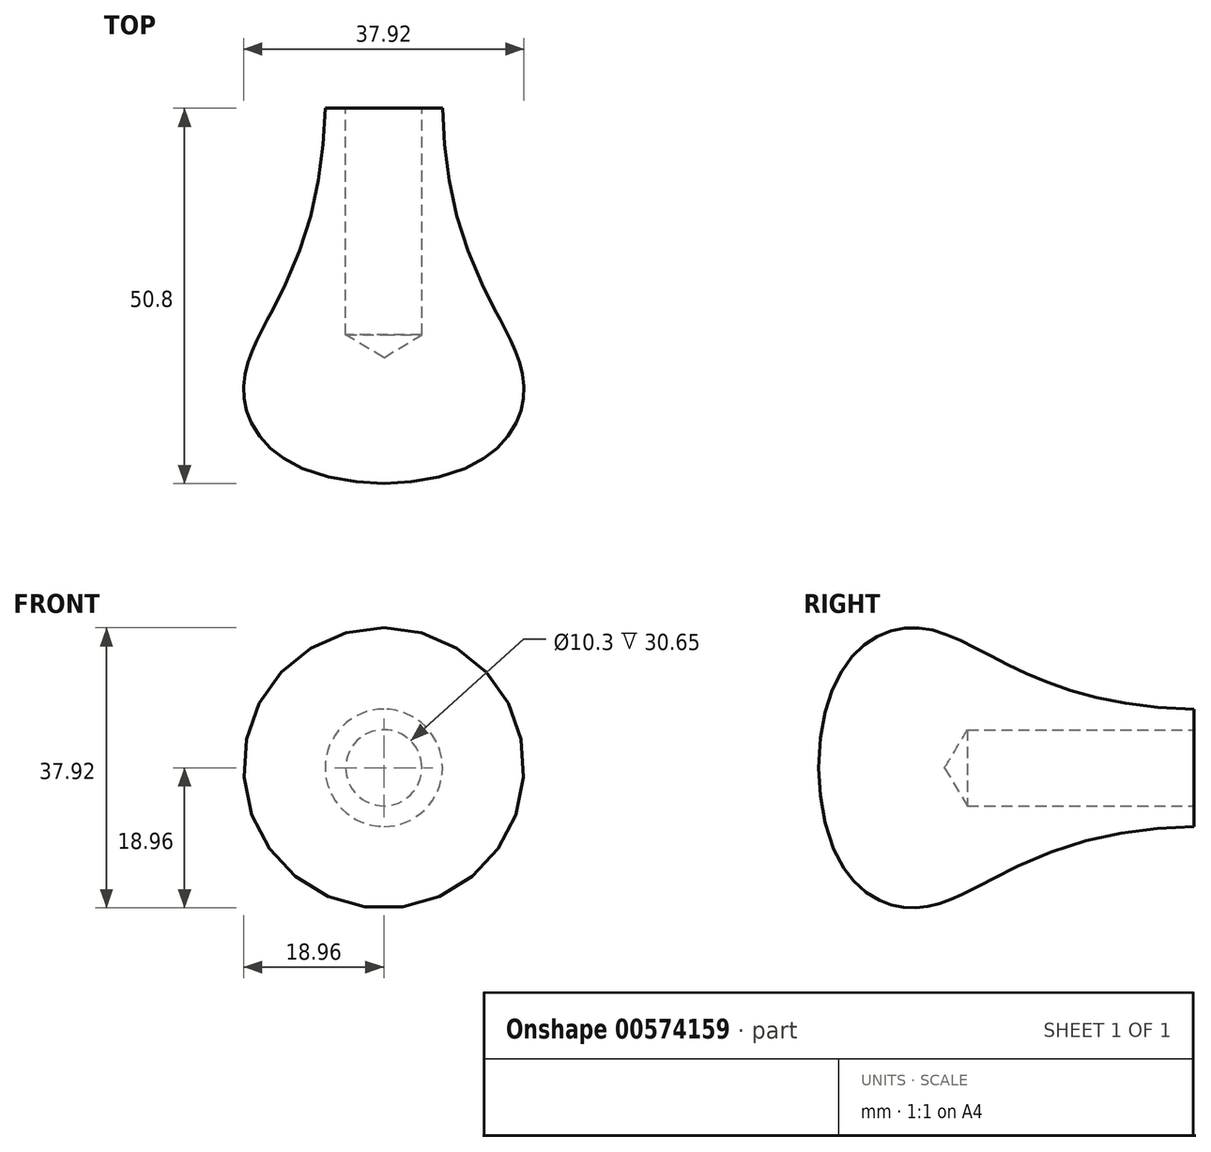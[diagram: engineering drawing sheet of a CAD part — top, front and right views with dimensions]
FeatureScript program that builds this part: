
annotation { "Feature Type Name" : "Feature", "Feature Type Description" : "" }
export const myFeature = defineFeature(function(context is Context, id is Id, definition is map)
    precondition{}
    {
        {
            var Q0;
            Q0=qCreatedBy(makeId("Right.planeOp"),FACE);
            var sketch = newSketch(context, id + "F0", { "sketchPlane" : qUnion([Q0])});
            skLineSegment(sketch, "E0", {"start": v(-50.8, 0) * mm, "end": v(0, 0) * mm});
            skLineSegment(sketch, "E1", {"start": v(0, 0) * mm, "end": v(0, 7.94) * mm});
            skFitSpline(sketch, "E2", {"points": [v(-50.8, 0) * mm, v(-37.12, 18.92) * mm, v(0, 7.94) * mm], "startDerivative": vector(1.84, 99.35) * mm, "endDerivative": vector(118.9, -2.3) * mm});
            skSolve(sketch);
        }
        {
            var Q0;
            Q0=makeQuery(id+"F0.imprint","IMPRINT",FACE,{"disambiguationData":[TD([[makeQuery(id+"F0.imprint","IMPRINT",EDGE,{"derivedFrom":sQuery(id+"F0.wireOp",EDGE,"E0")}),1.0]])]});
            var Q1;
            Q1=sQuery(id+"F0.wireOp",EDGE,"E0");
            revolve(context, id + "F1", {"entities" : qUnion([Q0]), "axis" : qUnion([Q1]), "revolveType" : RevolveType.FULL});
        }
        {
            var Q0;
            Q0=qCreatedBy(makeId("Front.planeOp"),FACE);
            var sketch = newSketch(context, id + "F2", { "sketchPlane" : qUnion([Q0])});
            skCircle(sketch, "E3", {"center": v(0, 0) * mm, "radius": 24.22 * mm, "construction": true});
            skSolve(sketch);
        }
        {
            var Q0;
            Q0=sQuery(id+"F2.wireOp",VERTEX,"E3.center");
            var Q1;
            Q1=makeQuery(id+"F1.opRevolve","SWEPT_BODY",BODY,{"disambiguationData":[OSD([sQuery(id+"F0.wireOp",EDGE,"E0"),sQuery(id+"F0.wireOp",EDGE,"E1"),sQuery(id+"F0.wireOp",EDGE,"E2")])]});
            hole(context, id + "F3", {"style" : HoleStyle.SIMPLE, "endStyle" : HoleEndStyle.BLIND, "oppositeDirection" : true, "standardTappedOrClearance" : lookupTablePath({ "standard" : "ISO", "engagement" : "75%", "pitch" : "1.75 mm", "size" : "M12", "type" : "Tapped" }), "standardBlindInLast" : lookupTablePath({ "standard" : "ISO", "engagement" : "75%", "pitch" : "1.75 mm", "size" : "M12", "type" : "Tapped" }), "holeDiameter" : 10.3 * mm, "showTappedDepth" : true, "holeDepth" : 30.65 * mm, "isTappedThrough" : true, "tappedDepth" : 25.4 * mm, "tapClearance" : 3, "locations" : qUnion([Q0]), "scope" : qUnion([Q1]), "majorDiameter" : 12 * mm});
        }
    });
